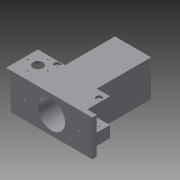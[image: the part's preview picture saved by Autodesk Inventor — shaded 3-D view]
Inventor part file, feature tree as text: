
AUTODESK INVENTOR PART (.ipt)
format: ipt  version: 2015 SP2 (Build 190223200, 223)  size: 230,912 bytes
history: native  units: mm
features: sketch x16, extrude x13, hole x3
ambient origin geometry x8: Origin, YZ Plane, XZ Plane, XY Plane, X Axis, Y Axis, Z Axis, Center Point
bodies: Body1 (feature_tree)
feature tree (32):
  extrude  "Extrusion2"  Depth=160.0mm TaperAngle=0.0deg
  extrude  "Extrusion10"  TaperAngle=0.0deg  [1 undecoded]
  extrude  "Extrusion11"  Depth=8.0mm
  extrude  "Extrusion12"  Depth=30.0mm
  hole  "Hole2"  [1 undecoded]
  hole  "Hole3"  [1 undecoded]
  extrude  "Extrusion15"  Depth=13.0mm
  hole  "Hole4"  [1 undecoded]
  extrude  "Extrusion16"  Depth=15.0mm
  extrude  "Extrusion17"  Depth=20.0mm
  extrude  "Extrusion18"  Depth=63.0mm TaperAngle=0.0deg
  extrude  "Extrusion21"  Depth=13.0mm
  extrude  "Extrusion22"  TaperAngle=0.0deg  [1 undecoded]
  extrude  "Extrusion23"  Depth=21.0mm
  extrude  "Extrusion24"  TaperAngle=0.0deg  [1 undecoded]
  extrude  "Extrusion25"  [1 undecoded]
  sketch  "Sketch4"  dims[d10=0.0mm d45=160.0mm d46=0.0mm]
  sketch  "Sketch18"  dims[d49=160.0mm d50=0.0mm d54=0.0mm]
  sketch  "Sketch19"  dims[d67=6.0mm d68=4.0mm d69=2.0mm d70=90.0deg d71=8.0mm d72=20.594885mm d74=31.0mm]
  sketch  "Sketch20"  dims[d77=6.0mm d78=4.0mm d79=2.0mm d80=90.0deg d81=8.0mm d82=20.594885mm d93=30.0mm]
  sketch  "Sketch23"  dims[d94=25.0mm d95=50.0mm d96=0.0mm]
  sketch  "Sketch24"  dims[d98=15.0mm]
  sketch  "Sketch27"  dims[d99=3.0mm d100=6.0mm d101=4.0mm d102=2.0mm d103=90.0deg d104=8.0mm d105=20.594885mm d109=50.0mm d110=0.0mm]
  sketch  "Sketch28"  dims[d113=0.0mm d114=13.0mm]
  sketch  "Sketch29"  dims[d115=5.0mm d116=0.0mm]
  sketch  "Sketch31"  dims[d126=45.0deg d127=15.0mm]
  sketch  "Sketch32"  dims[d130=63.0mm d131=0.0mm d132=20.0mm]
  sketch  "Sketch36"  dims[d133=20.0mm d134=63.0mm d135=0.0mm]
  sketch  "Sketch37"  dims[d136=63.0mm d137=0.0mm d138=13.0mm]
  sketch  "Sketch39"  dims[d139=5.0mm d140=0.0mm]
  sketch  "Sketch40"  dims[d144=10.0mm d145=21.0mm]
  sketch  "Sketch41"  dims[d146=5.0mm d147=0.0mm]
note: 7 required parameter values undecoded (feature->parameter linkage not recoverable at this tier; creation-order binding heuristic only, values carry confidence <= 0.55)
